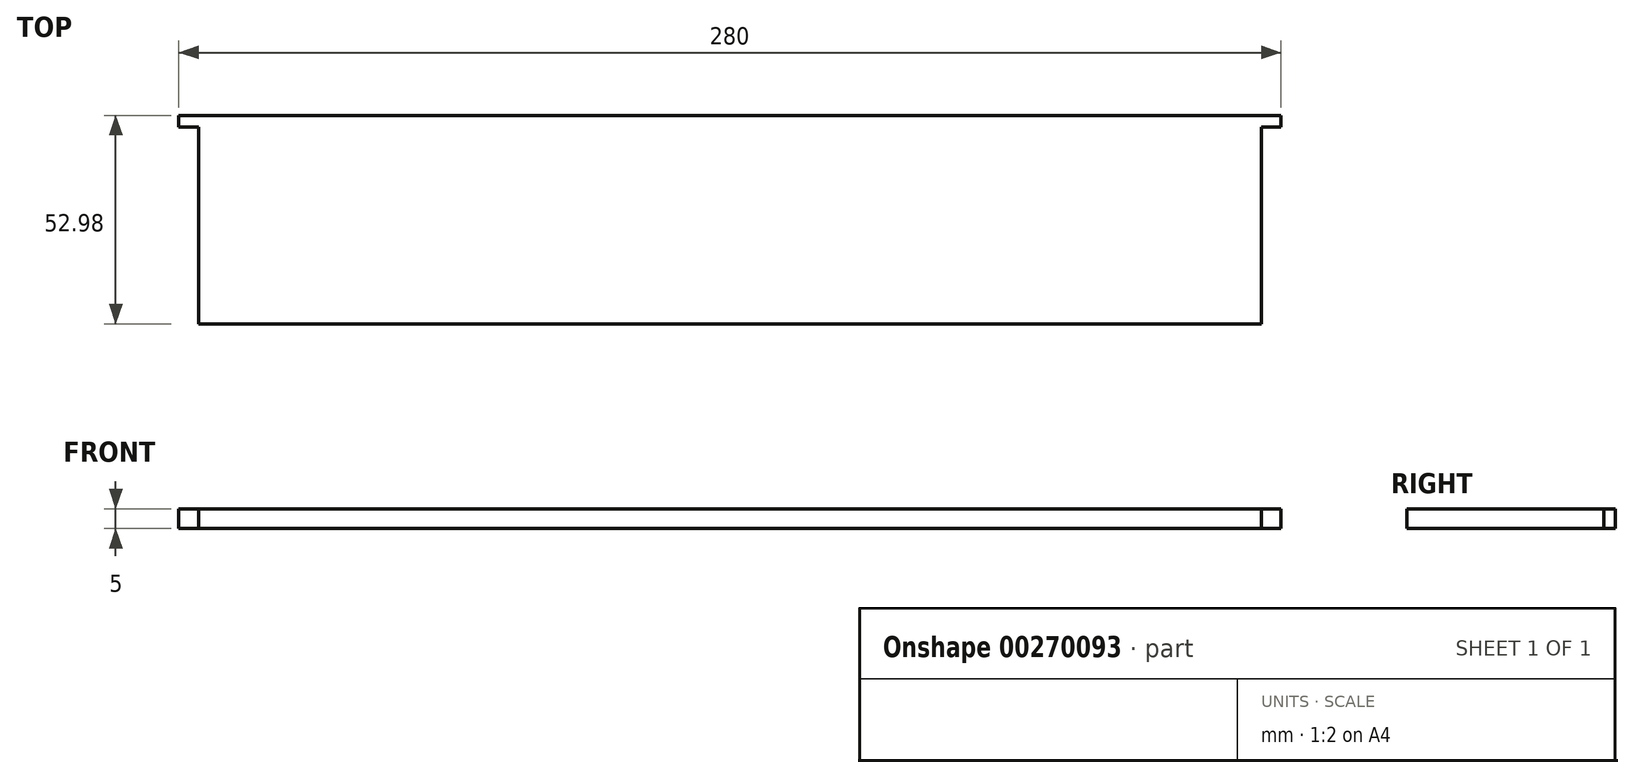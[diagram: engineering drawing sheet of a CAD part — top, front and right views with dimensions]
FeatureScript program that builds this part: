
annotation { "Feature Type Name" : "Feature", "Feature Type Description" : "" }
export const myFeature = defineFeature(function(context is Context, id is Id, definition is map)
    precondition{}
    {
        {
            var Q0;
            Q0=qCreatedBy(makeId("Top.planeOp"),FACE);
            var sketch = newSketch(context, id + "F0", { "sketchPlane" : qUnion([Q0])});
            skLineSegment(sketch, "E0.bottom", {"start": v(-135, 26.5) * mm, "end": v(135, 26.49) * mm});
            skLineSegment(sketch, "E0.top", {"start": v(-135, -26.49) * mm, "end": v(135, -26.5) * mm});
            skLineSegment(sketch, "E0.left", {"start": v(-135, 26.5) * mm, "end": v(-135, -26.5) * mm});
            skLineSegment(sketch, "E0.right", {"start": v(135, 26.5) * mm, "end": v(135, -26.5) * mm});
            skPoint(sketch, "E1", {"position": v(0, 26.5) * mm});
            skPoint(sketch, "E2", {"position": v(135, 0) * mm});
            skLineSegment(sketch, "E3", {"start": v(135, 26.49) * mm, "end": v(140, 26.49) * mm});
            skLineSegment(sketch, "E4", {"start": v(140, 26.5) * mm, "end": v(140, 23.49) * mm});
            skLineSegment(sketch, "E5", {"start": v(140, 23.49) * mm, "end": v(135, 23.49) * mm});
            skLineSegment(sketch, "E6", {"start": v(-135, 26.5) * mm, "end": v(-140, 26.5) * mm});
            skLineSegment(sketch, "E7", {"start": v(-140, 26.5) * mm, "end": v(-140, 23.49) * mm});
            skLineSegment(sketch, "E8", {"start": v(-140, 23.49) * mm, "end": v(-135, 23.49) * mm});
            skSolve(sketch);
        }
        {
            var Q0;
            Q0=makeQuery(id+"F0.imprint","IMPRINT",FACE,{"disambiguationData":[TD([[makeQuery(id+"F0.imprint","IMPRINT",EDGE,{"derivedFrom":sQuery(id+"F0.wireOp",EDGE,"E0.bottom")}),-1.0]])]});
            var Q1;
            {var subQ0=sQuery(id+"F0.wireOp",EDGE,"E3");Q1=makeQuery(id+"F0.imprint","IMPRINT",FACE,{"disambiguationData":[TD([[makeQuery(id+"F0.imprint","IMPRINT",EDGE,{"derivedFrom":subQ0}),-1.0]])]});}
            var Q2;
            {var subQ0=sQuery(id+"F0.wireOp",EDGE,"E6");Q2=makeQuery(id+"F0.imprint","IMPRINT",FACE,{"disambiguationData":[TD([[makeQuery(id+"F0.imprint","IMPRINT",EDGE,{"derivedFrom":subQ0}),1.0]])]});}
            extrude(context, id + "F1", {"entities" : qUnion([Q0, Q1, Q2]), "depth" : 5 * mm, "symmetric" : true});
        }
    });
